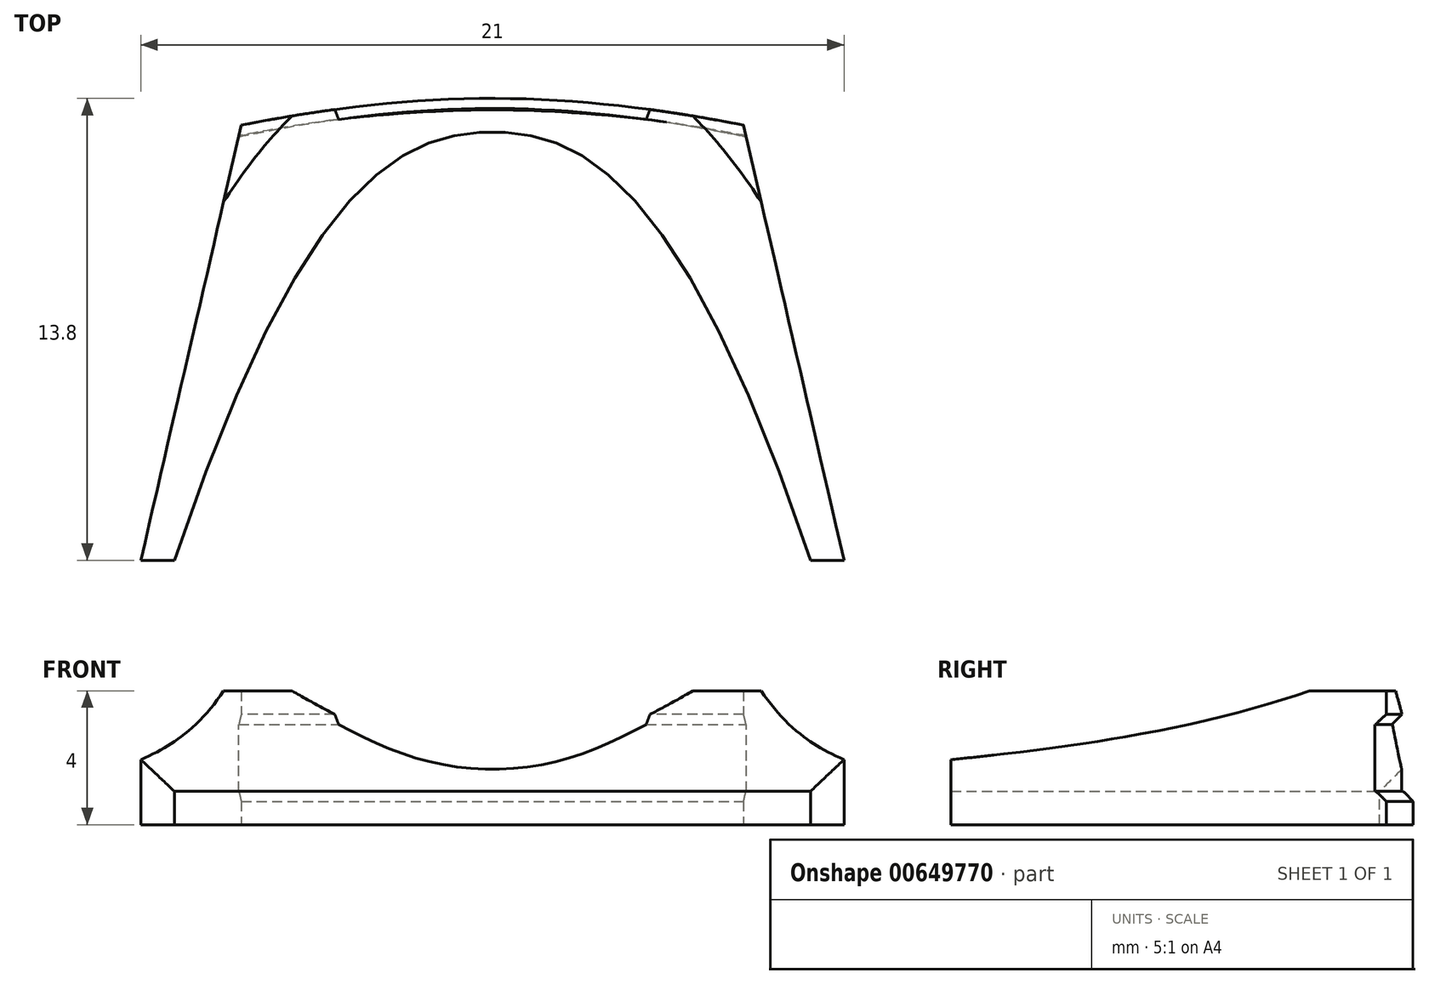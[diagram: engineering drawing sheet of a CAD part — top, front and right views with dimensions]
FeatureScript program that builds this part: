
annotation { "Feature Type Name" : "Feature", "Feature Type Description" : "" }
export const myFeature = defineFeature(function(context is Context, id is Id, definition is map)
    precondition{}
    {
        {
            var Q0;
            Q0=qCreatedBy(makeId("Top.planeOp"),FACE);
            var sketch = newSketch(context, id + "F0", { "sketchPlane" : qUnion([Q0])});
            skLineSegment(sketch, "E0", {"start": v(-7.5, 0) * mm, "end": v(7.5, 0) * mm});
            skLineSegment(sketch, "E1", {"start": v(-10.5, -13) * mm, "end": v(10.5, -13) * mm});
            skPoint(sketch, "E2", {"position": v(0, -13) * mm});
            skLineSegment(sketch, "E3", {"start": v(-7.5, 0) * mm, "end": v(-10.5, -13) * mm});
            skLineSegment(sketch, "E4", {"start": v(7.5, 0) * mm, "end": v(10.5, -13) * mm});
            skFitSpline(sketch, "E5", {"points": [v(-7.5, 0) * mm, v(0, 0.8) * mm, v(7.5, 0) * mm], "startDerivative": vector(15, 2.97) * mm, "endDerivative": vector(15, -2.97) * mm});
            skFitSpline(sketch, "E6.0", {"points": [v(-7.81, 1.57) * mm, v(-6.52, 1.82) * mm, v(-4.58, 2.14) * mm, v(-1.97, 2.36) * mm, v(0, 2.42) * mm, v(1.97, 2.36) * mm, v(4.58, 2.14) * mm, v(6.52, 1.82) * mm, v(7.81, 1.57) * mm]});
            skFitSpline(sketch, "E7", {"points": [v(-9.5, -13) * mm, v(0, -0.2) * mm, v(9.5, -13) * mm], "startDerivative": vector(22.07, 65.71) * mm, "endDerivative": vector(22.07, -65.71) * mm});
            skLineSegment(sketch, "E8", {"start": v(-5.82, -2.05) * mm, "end": v(5.82, -2.05) * mm, "construction": true});
            skLineSegment(sketch, "E9", {"start": v(0, -2.05) * mm, "end": v(0, -0.2) * mm, "construction": true});
            skLineSegment(sketch, "E10", {"start": v(0, -0.2) * mm, "end": v(0, 0.8) * mm, "construction": true});
            skSolve(sketch);
        }
        {
            var Q0;
            Q0=makeQuery(id+"F0.imprint","IMPRINT",FACE,{"disambiguationData":[TD([[makeQuery(id+"F0.imprint","IMPRINT",EDGE,{"derivedFrom":sQuery(id+"F0.wireOp",EDGE,"E0")}),-1.0]])]});
            var Q1;
            Q1=makeQuery(id+"F0.imprint","IMPRINT",FACE,{"disambiguationData":[TD([[makeQuery(id+"F0.imprint","IMPRINT",EDGE,{"derivedFrom":sQuery(id+"F0.wireOp",EDGE,"E0")}),1.0]])]});
            extrude(context, id + "F1", {"entities" : qUnion([Q0, Q1]), "depth" : 4 * mm, "offsetDistance" : 25 * mm});
        }
        {
            var Q0;
            Q0=makeQuery(id+"F1.opExtrude","CAP_EDGE",EDGE,{"disambiguationData":[OSD([sQuery(id+"F0.wireOp",EDGE,"E7")])],"isStart":false});
            chamfer(context, id + "F2", {"entities" : qUnion([Q0]), "width" : 3 * mm, "tangentPropagation" : true});
        }
        {
            var Q0;
            Q0=sQuery(id+"F0.wireOp",EDGE,"E5");
            cPoint(context, id + "F3", {"entities" : qUnion([Q0]), "parameter" : 0.5});
        }
        {
            var Q0;
            Q0=sQuery(id+"F0.wireOp",EDGE,"E10");
            var Q1;
            Q1 = qCreatedBy(id + "F3" ,VERTEX);
            cPlane(context, id + "F4", {"entities" : qUnion([Q0, Q1]), "cplaneType" : CPlaneType.CURVE_POINT, "offset" : 25 * mm, "width" : 150 * mm, "height" : 150 * mm});
        }
        {
            var Q0;
            Q0=sQuery(id+"F0.wireOp",EDGE,"E6.0");
            extrude(context, id + "F5", {"bodyType" : ToolBodyType.SURFACE, "surfaceEntities" : qUnion([Q0]), "depth" : 2 * mm, "offsetDistance" : 25 * mm});
        }
        {
            var Q0;
            Q0=makeQuery(id+"F5.opExtrude","SWEPT_BODY",BODY,{"disambiguationData":[OSD([sQuery(id+"F0.wireOp",EDGE,"E6.0")])]});
            transform(context, id + "F6", {"entities" : qUnion([Q0]), "transformType" : TransformType.TRANSLATION_3D, "dx" : 0 * mm, "dy" : 0 * mm, "dz" : 1 * mm, "makeCopy" : false});
        }
        {
            var Q0;
            Q0=qCreatedBy(id+"F4.planeOp",FACE);
            cPlane(context, id + "F7", {"entities" : qUnion([Q0]), "cplaneType" : CPlaneType.OFFSET, "offset" : 5 * mm, "width" : 150 * mm, "height" : 150 * mm});
        }
        {
            var Q0;
            Q0=qCreatedBy(id+"F7.planeOp",FACE);
            var sketch = newSketch(context, id + "F8", { "sketchPlane" : qUnion([Q0])});
            skFitSpline(sketch, "E11.0.0", {"points": [v(-7.82, 3) * mm, v(-6.54, 3) * mm, v(-4.6, 3) * mm, v(-1.99, 3) * mm, v(-0.02, 3) * mm, v(1.95, 3) * mm, v(4.56, 3) * mm, v(6.5, 3) * mm, v(7.8, 3) * mm]});
            skLineSegment(sketch, "E11.0.1", {"start": v(7.8, 3) * mm, "end": v(7.8, 1) * mm});
            skFitSpline(sketch, "E11.0.2", {"points": [v(7.8, 1) * mm, v(6.5, 1) * mm, v(4.56, 1) * mm, v(1.95, 1) * mm, v(-0.02, 1) * mm, v(-1.99, 1) * mm, v(-4.6, 1) * mm, v(-6.54, 1) * mm, v(-7.82, 1) * mm]});
            skLineSegment(sketch, "E11.0.3", {"start": v(-7.82, 1) * mm, "end": v(-7.82, 3) * mm});
            skSolve(sketch);
        }
        {
            var Q0;
            Q0=makeQuery(id+"F8.imprint","IMPRINT",FACE,{"disambiguationData":[TD([[makeQuery(id+"F8.imprint","IMPRINT",EDGE,{"derivedFrom":sQuery(id+"F8.wireOp",EDGE,"E11.0.0")}),-1.0]])]});
            var Q1;
            Q1=makeQuery(id+"F5.opExtrude","SWEPT_FACE",FACE,{"disambiguationData":[OSD([sQuery(id+"F0.wireOp",EDGE,"E6.0")])]});
            extrude(context, id + "F9", {"entities" : qUnion([Q0]), "endBound" : BoundingType.UP_TO_SURFACE, "oppositeDirection" : true, "depth" : 25 * mm, "endBoundEntityFace" : qUnion([Q1]), "offsetDistance" : 25 * mm});
        }
        {
            var Q0;
            Q0=makeQuery(id+"F9.opExtrude","SWEPT_BODY",BODY,{"disambiguationData":[OSD([sQuery(id+"F8.wireOp",EDGE,"E11.0.0"),sQuery(id+"F8.wireOp",EDGE,"E11.0.1"),sQuery(id+"F8.wireOp",EDGE,"E11.0.2"),sQuery(id+"F8.wireOp",EDGE,"E11.0.3")])]});
            transform(context, id + "F10", {"entities" : qUnion([Q0]), "transformType" : TransformType.TRANSLATION_3D, "dx" : 0 * mm, "dy" : -1.96 * mm, "dz" : 0 * mm, "makeCopy" : false});
        }
        {
            var Q0;
            Q0=makeQuery(id+"F9.opExtrude","SWEPT_BODY",BODY,{"disambiguationData":[OSD([sQuery(id+"F8.wireOp",EDGE,"E11.0.0"),sQuery(id+"F8.wireOp",EDGE,"E11.0.1"),sQuery(id+"F8.wireOp",EDGE,"E11.0.2"),sQuery(id+"F8.wireOp",EDGE,"E11.0.3")])]});
            var Q1;
            Q1=makeQuery(id+"F1.opExtrude","SWEPT_BODY",BODY,{"disambiguationData":[OSD([sQuery(id+"F0.wireOp",EDGE,"E1"),sQuery(id+"F0.wireOp",EDGE,"E3"),sQuery(id+"F0.wireOp",EDGE,"E4"),sQuery(id+"F0.wireOp",EDGE,"E5"),sQuery(id+"F0.wireOp",EDGE,"E7")])]});
            booleanBodies(context, id + "F11", {"operationType" : BooleanOperationType.SUBTRACTION, "tools" : qUnion([Q0]), "targets" : qUnion([Q1])});
        }
        {
            var Q0;
            Q0=makeQuery(id+"F11.opBoolean","INTERSECT",EDGE,{"disambiguationData":[OD(1.0)],"derivedFrom":[makeQuery(id+"F1.opExtrude","SWEPT_FACE",FACE,{"disambiguationData":[OSD([sQuery(id+"F0.wireOp",EDGE,"E5")])]}),makeQuery(id+"F9.opExtrude","SWEPT_FACE",FACE,{"disambiguationData":[OSD([sQuery(id+"F8.wireOp",EDGE,"E11.0.0")])]})]});
            var Q1;
            Q1=makeQuery(id+"F11.opBoolean","INTERSECT",EDGE,{"derivedFrom":[makeQuery(id+"F1.opExtrude","SWEPT_FACE",FACE,{"disambiguationData":[OSD([sQuery(id+"F0.wireOp",EDGE,"E5")])]}),makeQuery(id+"F9.opExtrude","SWEPT_FACE",FACE,{"disambiguationData":[OSD([sQuery(id+"F8.wireOp",EDGE,"E11.0.2")])]})]});
            var Q2;
            Q2=makeQuery(id+"F11.opBoolean","INTERSECT",EDGE,{"disambiguationData":[OD(0.0)],"derivedFrom":[makeQuery(id+"F1.opExtrude","SWEPT_FACE",FACE,{"disambiguationData":[OSD([sQuery(id+"F0.wireOp",EDGE,"E5")])]}),makeQuery(id+"F9.opExtrude","SWEPT_FACE",FACE,{"disambiguationData":[OSD([sQuery(id+"F8.wireOp",EDGE,"E11.0.0")])]})]});
            chamfer(context, id + "F12", {"entities" : qUnion([Q0, Q1, Q2]), "width" : .3 * mm, "tangentPropagation" : true});
        }
    });
